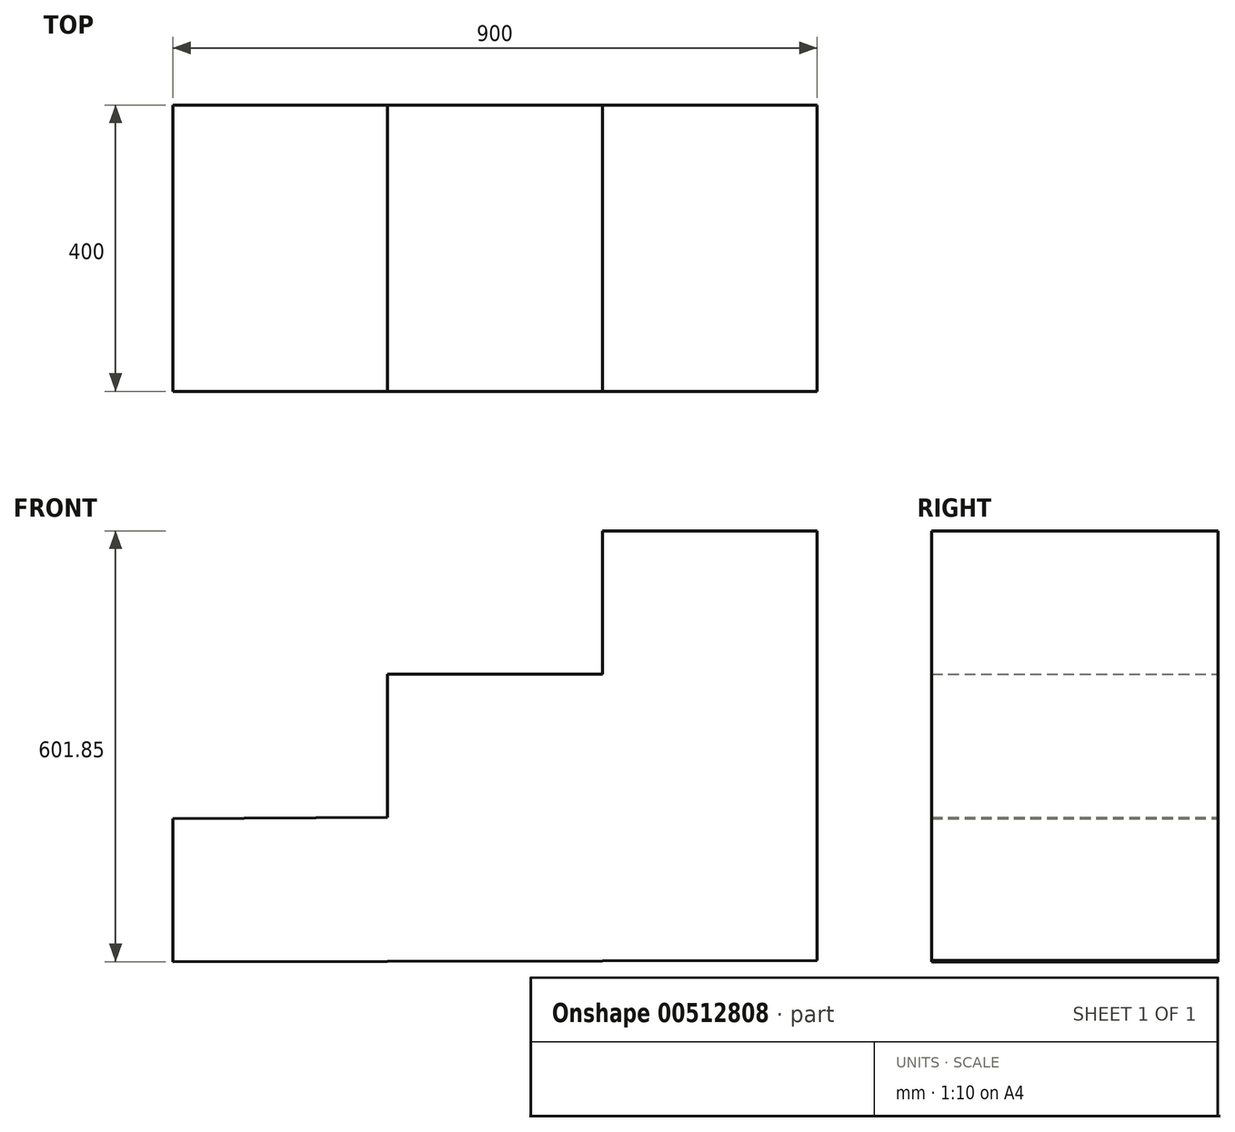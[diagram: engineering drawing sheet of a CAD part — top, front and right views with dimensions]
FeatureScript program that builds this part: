
annotation { "Feature Type Name" : "Feature", "Feature Type Description" : "" }
export const myFeature = defineFeature(function(context is Context, id is Id, definition is map)
    precondition{}
    {
        {
            var Q0;
            Q0=qCreatedBy(makeId("Front.planeOp"),FACE);
            var sketch = newSketch(context, id + "F0", { "sketchPlane" : qUnion([Q0])});
            skLineSegment(sketch, "E0", {"start": v(623.06, 335.44) * mm, "end": v(623.06, -264.56) * mm});
            skLineSegment(sketch, "E1", {"start": v(323.06, 335.44) * mm, "end": v(623.06, 335.44) * mm});
            skLineSegment(sketch, "E2", {"start": v(323.06, 335.44) * mm, "end": v(323.06, 135.44) * mm});
            skLineSegment(sketch, "E3", {"start": v(323.06, 135.44) * mm, "end": v(23.06, 135.44) * mm});
            skLineSegment(sketch, "E4", {"start": v(23.06, 135.44) * mm, "end": v(23.06, -64.56) * mm});
            skLineSegment(sketch, "E5", {"start": v(23.06, -64.56) * mm, "end": v(-276.93, -66.4) * mm});
            skLineSegment(sketch, "E6", {"start": v(-276.93, -66.4) * mm, "end": v(-276.94, -266.4) * mm});
            skLineSegment(sketch, "E7", {"start": v(-276.94, -266.4) * mm, "end": v(623.06, -264.56) * mm});
            skSolve(sketch);
        }
        {
            var Q0;
            Q0=makeQuery(id+"F0.imprint","IMPRINT",FACE,{"disambiguationData":[TD([[makeQuery(id+"F0.imprint","IMPRINT",EDGE,{"derivedFrom":sQuery(id+"F0.wireOp",EDGE,"E0")}),-1.0]])]});
            extrude(context, id + "F1", {"entities" : qUnion([Q0]), "depth" : 400 * mm});
        }
    });
